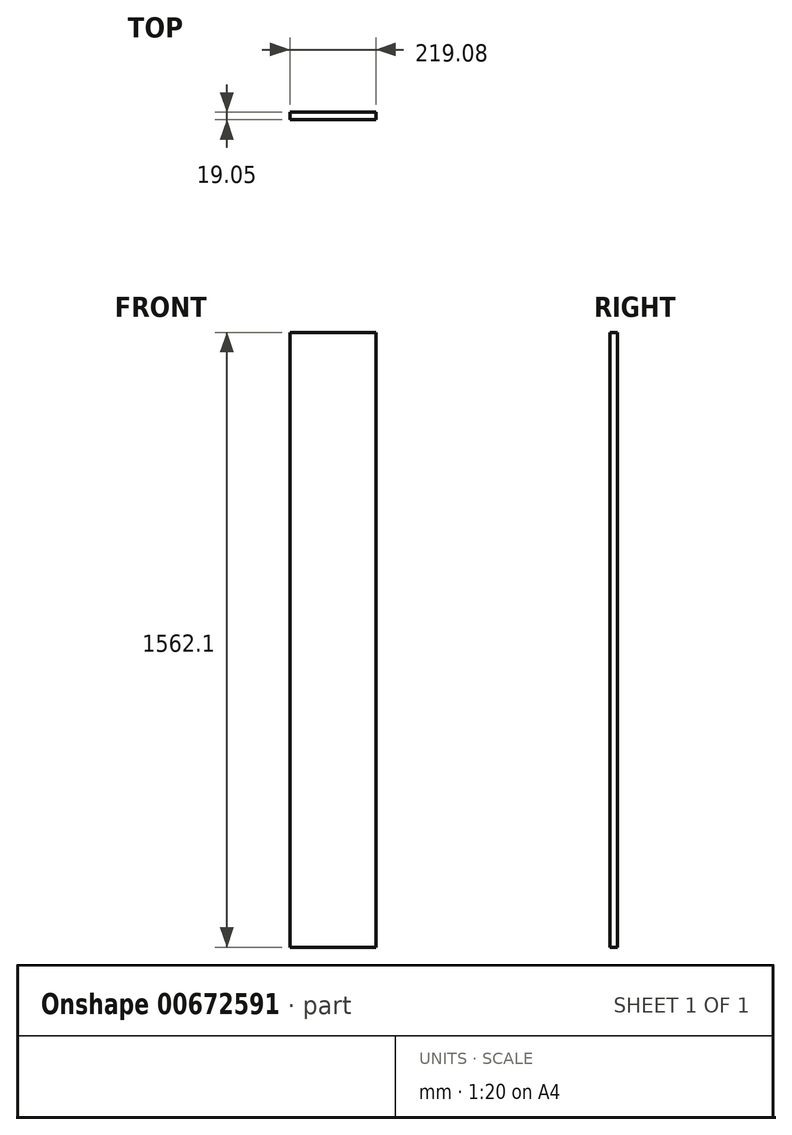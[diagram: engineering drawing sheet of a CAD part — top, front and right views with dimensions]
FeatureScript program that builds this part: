
annotation { "Feature Type Name" : "Feature", "Feature Type Description" : "" }
export const myFeature = defineFeature(function(context is Context, id is Id, definition is map)
    precondition{}
    {
        {
            var Q0;
            Q0=qCreatedBy(makeId("Front.planeOp"),FACE);
            var sketch = newSketch(context, id + "F0", { "sketchPlane" : qUnion([Q0])});
            skLineSegment(sketch, "E0.bottom", {"start": v(109.54, 781.05) * mm, "end": v(-109.54, 781.05) * mm});
            skLineSegment(sketch, "E0.top", {"start": v(109.54, -781.05) * mm, "end": v(-109.54, -781.05) * mm});
            skLineSegment(sketch, "E0.left", {"start": v(109.54, 781.05) * mm, "end": v(109.54, -781.05) * mm});
            skLineSegment(sketch, "E0.right", {"start": v(-109.54, 781.05) * mm, "end": v(-109.54, -781.05) * mm});
            skPoint(sketch, "E0.middle", {"position": v(0, 0) * mm});
            skSolve(sketch);
        }
        {
            var Q0;
            Q0=makeQuery(id+"F0.imprint","IMPRINT",FACE,{"disambiguationData":[TD([[makeQuery(id+"F0.imprint","IMPRINT",EDGE,{"derivedFrom":sQuery(id+"F0.wireOp",EDGE,"E0.bottom")}),1.0]])]});
            extrude(context, id + "F1", {"entities" : qUnion([Q0]), "depth" : 19.05 * mm, "offsetDistance" : 25.4 * mm});
        }
    });
